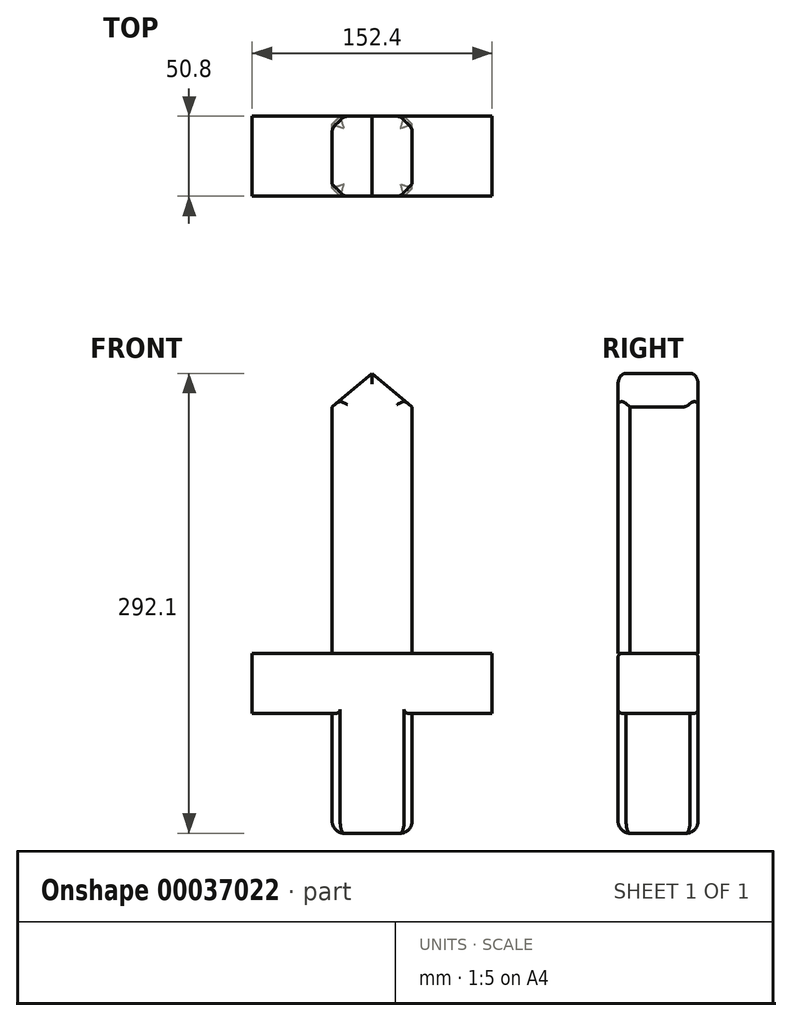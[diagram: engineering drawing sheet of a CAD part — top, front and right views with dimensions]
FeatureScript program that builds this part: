
annotation { "Feature Type Name" : "Feature", "Feature Type Description" : "" }
export const myFeature = defineFeature(function(context is Context, id is Id, definition is map)
    precondition{}
    {
        {
            var Q0;
            Q0=qCreatedBy(makeId("Top.planeOp"),FACE);
            var sketch = newSketch(context, id + "F0", { "sketchPlane" : qUnion([Q0])});
            skLineSegment(sketch, "E0.bottom", {"start": v(0, 0) * mm, "end": v(50.8, 0) * mm});
            skLineSegment(sketch, "E0.top", {"start": v(0, 50.8) * mm, "end": v(50.8, 50.8) * mm});
            skLineSegment(sketch, "E0.left", {"start": v(0, 0) * mm, "end": v(0, 50.8) * mm});
            skLineSegment(sketch, "E0.right", {"start": v(50.8, 0) * mm, "end": v(50.8, 50.8) * mm});
            skSolve(sketch);
        }
        {
            var Q0;
            Q0 = qSketchRegion(id + "F0", true);
            extrude(context, id + "F1", {"entities" : qUnion([Q0]), "depth" : 76.2 * mm});
        }
        {
            var Q0;
            Q0=makeQuery(id+"F1.opExtrude","CAP_FACE",FACE,{"disambiguationData":[OSD([sQuery(id+"F0.wireOp",EDGE,"E0.bottom"),sQuery(id+"F0.wireOp",EDGE,"E0.top"),sQuery(id+"F0.wireOp",EDGE,"E0.left"),sQuery(id+"F0.wireOp",EDGE,"E0.right")])],"isStart":false});
            var sketch = newSketch(context, id + "F2", { "sketchPlane" : qUnion([Q0])});
            skLineSegment(sketch, "E1.bottom", {"start": v(0, 0) * mm, "end": v(50.8, 0) * mm});
            skLineSegment(sketch, "E1.top", {"start": v(0, 50.8) * mm, "end": v(50.8, 50.8) * mm});
            skLineSegment(sketch, "E1.left", {"start": v(0, 0) * mm, "end": v(0, 50.8) * mm});
            skLineSegment(sketch, "E1.right", {"start": v(50.8, 0) * mm, "end": v(50.8, 50.8) * mm});
            skLineSegment(sketch, "E2.rect.bottom", {"start": v(101.6, 0) * mm, "end": v(-50.8, 0) * mm});
            skLineSegment(sketch, "E2.rect.top", {"start": v(101.6, 50.8) * mm, "end": v(-50.8, 50.8) * mm});
            skLineSegment(sketch, "E2.rect.left", {"start": v(101.6, 0) * mm, "end": v(101.6, 50.8) * mm});
            skLineSegment(sketch, "E2.rect.right", {"start": v(-50.8, 0) * mm, "end": v(-50.8, 50.8) * mm});
            skPoint(sketch, "E2.rect.middle", {"position": v(25.4, 25.4) * mm});
            skPoint(sketch, "E2.rect.middle.positionSnap0", {"position": v(50.8, 25.4) * mm});
            skPoint(sketch, "E2.rect.middle.positionSnap1", {"position": v(25.4, 50.8) * mm});
            skPoint(sketch, "E2.rect.centerSnap0", {"position": v(50.8, 25.4) * mm});
            skPoint(sketch, "E2.rect.centerSnap1", {"position": v(25.4, 50.8) * mm});
            skSolve(sketch);
        }
        {
            var Q0;
            {var subQ2=sQuery(id+"F2.wireOp",EDGE,"E1.left");Q0=makeQuery(id+"F2.imprint","IMPRINT",FACE,{"disambiguationData":[TD([[makeQuery(id+"F2.imprint","IMPRINT",EDGE,{"derivedFrom":subQ2}),1.0]])]});}
            var Q1;
            {var subQ2=sQuery(id+"F2.wireOp",EDGE,"E1.left");Q1=makeQuery(id+"F2.imprint","IMPRINT",FACE,{"disambiguationData":[TD([[makeQuery(id+"F2.imprint","IMPRINT",EDGE,{"derivedFrom":subQ2}),-1.0]])]});}
            var Q2;
            {var subQ2=sQuery(id+"F2.wireOp",EDGE,"E1.right");Q2=makeQuery(id+"F2.imprint","IMPRINT",FACE,{"disambiguationData":[TD([[makeQuery(id+"F2.imprint","IMPRINT",EDGE,{"derivedFrom":subQ2}),-1.0]])]});}
            extrude(context, id + "F3", {"entities" : qUnion([Q0, Q1, Q2]), "operationType" : NewBodyOperationType.ADD, "depth" : 38.1 * mm});
        }
        {
            var Q0;
            Q0=makeQuery(id+"F3.boolean.opBoolean","MERGE",FACE,{"derivedFrom":[makeQuery(id+"F1.opExtrude","SWEPT_FACE",FACE,{"disambiguationData":[OSD([sQuery(id+"F0.wireOp",EDGE,"E0.bottom")])]}),makeQuery(id+"F3.opExtrude","SWEPT_FACE",FACE,{"disambiguationData":[OSD([sQuery(id+"F2.wireOp",EDGE,"E2.rect.bottom")])]})]});
            var sketch = newSketch(context, id + "F4", { "sketchPlane" : qUnion([Q0])});
            skLineSegment(sketch, "E3.bottom", {"start": v(0, 114.3) * mm, "end": v(50.8, 114.3) * mm});
            skLineSegment(sketch, "E3.left", {"start": v(0, 114.3) * mm, "end": v(0, 270.79) * mm});
            skLineSegment(sketch, "E3.right", {"start": v(50.8, 114.3) * mm, "end": v(50.8, 270.79) * mm});
            skLineSegment(sketch, "E4", {"start": v(25.4, 292.1) * mm, "end": v(0, 270.79) * mm});
            skLineSegment(sketch, "E5", {"start": v(25.4, 292.1) * mm, "end": v(50.8, 270.79) * mm});
            skPoint(sketch, "E6.orphan", {"position": v(0, 292.1) * mm});
            skPoint(sketch, "E3.top.end.orphan", {"position": v(50.8, 292.1) * mm});
            skSolve(sketch);
        }
        {
            var Q0;
            Q0=makeQuery(id+"F4.imprint","IMPRINT",FACE,{"disambiguationData":[TD([[makeQuery(id+"F4.imprint","IMPRINT",EDGE,{"derivedFrom":sQuery(id+"F4.wireOp",EDGE,"E3.bottom")}),-1.0]])]});
            extrude(context, id + "F5", {"entities" : qUnion([Q0]), "oppositeDirection" : true, "depth" : 50.8 * mm});
        }
        {
            var Q0;
            Q0=makeQuery(id+"F5.opExtrude","CAP_EDGE",EDGE,{"disambiguationData":[OSD([sQuery(id+"F4.wireOp",EDGE,"E3.left")])],"isStart":false});
            var Q1;
            Q1=makeQuery(id+"F5.opExtrude","CAP_EDGE",EDGE,{"disambiguationData":[OSD([sQuery(id+"F4.wireOp",EDGE,"E3.right")])],"isStart":false});
            var Q2;
            Q2=makeQuery(id+"F5.opExtrude","CAP_EDGE",EDGE,{"disambiguationData":[OSD([sQuery(id+"F4.wireOp",EDGE,"E3.left")])],"isStart":true});
            var Q3;
            Q3=makeQuery(id+"F5.opExtrude","CAP_EDGE",EDGE,{"disambiguationData":[OSD([sQuery(id+"F4.wireOp",EDGE,"E3.right")])],"isStart":true});
            chamfer(context, id + "F6", {"entities" : qUnion([Q0, Q1, Q2, Q3]), "width" : 7.62 * mm, "tangentPropagation" : true});
        }
        {
            var Q0;
            Q0=makeQuery(id+"F1.opExtrude","CAP_FACE",FACE,{"disambiguationData":[OSD([sQuery(id+"F0.wireOp",EDGE,"E0.bottom"),sQuery(id+"F0.wireOp",EDGE,"E0.top"),sQuery(id+"F0.wireOp",EDGE,"E0.left"),sQuery(id+"F0.wireOp",EDGE,"E0.right")])],"isStart":true});
            var sketch = newSketch(context, id + "F7", { "sketchPlane" : qUnion([Q0])});
            skLineSegment(sketch, "E7", {"start": v(25.4, 0) * mm, "end": v(25.4, -50.8) * mm, "construction": true});
            skArc(sketch, "E8", {"start": v(25.4, -50.8) * mm, "mid": v(50.8, -25.4) * mm, "end": v(25.4, 0) * mm});
            skSolve(sketch);
        }
        {
            var Q0;
            Q0=sQuery(id+"F7.wireOp",EDGE,"E8");
            var Q1;
            Q1=sQuery(id+"F7.wireOp",EDGE,"E7");
            revolve(context, id + "F8", {"bodyType" : ToolBodyType.SURFACE, "surfaceEntities" : qUnion([Q0]), "axis" : qUnion([Q1]), "revolveType" : RevolveType.FULL});
        }
        {
            var Q0;
            Q0=makeQuery(id+"F1.opExtrude","CAP_EDGE",EDGE,{"disambiguationData":[OSD([sQuery(id+"F0.wireOp",EDGE,"E0.right")])],"isStart":true});
            var Q1;
            Q1=makeQuery(id+"F1.opExtrude","CAP_EDGE",EDGE,{"disambiguationData":[OSD([sQuery(id+"F0.wireOp",EDGE,"E0.bottom")])],"isStart":true});
            var Q2;
            Q2=makeQuery(id+"F1.opExtrude","CAP_EDGE",EDGE,{"disambiguationData":[OSD([sQuery(id+"F0.wireOp",EDGE,"E0.left")])],"isStart":true});
            var Q3;
            Q3=makeQuery(id+"F1.opExtrude","CAP_EDGE",EDGE,{"disambiguationData":[OSD([sQuery(id+"F0.wireOp",EDGE,"E0.top")])],"isStart":true});
            fillet(context, id + "F9", {"entities" : qUnion([Q0, Q1, Q2, Q3]), "radius" : 7.62 * mm, "tangentPropagation" : true, "allowEdgeOverflow" : false});
        }
        {
            var Q0;
            Q0=makeQuery(id+"F1.opExtrude","SWEPT_EDGE",EDGE,{"disambiguationData":[OSD([sQuery(id+"F0.wireOp",EDGE,"E0.top"),sQuery(id+"F0.wireOp",EDGE,"E0.left")])]});
            var Q1;
            Q1=makeQuery(id+"F1.opExtrude","SWEPT_EDGE",EDGE,{"disambiguationData":[OSD([sQuery(id+"F0.wireOp",EDGE,"E0.top"),sQuery(id+"F0.wireOp",EDGE,"E0.right")])]});
            var Q2;
            Q2=makeQuery(id+"F1.opExtrude","SWEPT_EDGE",EDGE,{"disambiguationData":[OSD([sQuery(id+"F0.wireOp",EDGE,"E0.bottom"),sQuery(id+"F0.wireOp",EDGE,"E0.left")])]});
            var Q3;
            Q3=makeQuery(id+"F1.opExtrude","SWEPT_EDGE",EDGE,{"disambiguationData":[OSD([sQuery(id+"F0.wireOp",EDGE,"E0.bottom"),sQuery(id+"F0.wireOp",EDGE,"E0.right")])]});
            chamfer(context, id + "F10", {"entities" : qUnion([Q0, Q1, Q2, Q3]), "width" : 5.08 * mm, "tangentPropagation" : true});
        }
        {
            var Q0;
            Q0=makeQuery(id+"F3.opExtrude","CAP_EDGE",EDGE,{"disambiguationData":[OSD([sQuery(id+"F2.wireOp",EDGE,"E2.rect.top")])],"isStart":false});
            var Q1;
            {var subQ0=sQuery(id+"F2.wireOp",EDGE,"E2.rect.top");Q1=makeQuery(id+"F3.boolean.opBoolean","SPLIT",EDGE,{"disambiguationData":[TD([makeQuery(id+"F1.opExtrude","SWEPT_FACE",FACE,{"disambiguationData":[OSD([sQuery(id+"F0.wireOp",EDGE,"E0.left")])]})])],"derivedFrom":makeQuery(id+"F3.opExtrude","CAP_EDGE",EDGE,{"disambiguationData":[OSD([subQ0])],"isStart":true})});}
            var Q2;
            {var subQ0=sQuery(id+"F2.wireOp",EDGE,"E2.rect.top");Q2=makeQuery(id+"F3.boolean.opBoolean","SPLIT",EDGE,{"disambiguationData":[TD([makeQuery(id+"F1.opExtrude","SWEPT_FACE",FACE,{"disambiguationData":[OSD([sQuery(id+"F0.wireOp",EDGE,"E0.right")])]})])],"derivedFrom":makeQuery(id+"F3.opExtrude","CAP_EDGE",EDGE,{"disambiguationData":[OSD([subQ0])],"isStart":true})});}
            var Q3;
            Q3=makeQuery(id+"F3.opExtrude","CAP_EDGE",EDGE,{"disambiguationData":[OSD([sQuery(id+"F2.wireOp",EDGE,"E2.rect.bottom")])],"isStart":false});
            var Q4;
            {var subQ0=sQuery(id+"F2.wireOp",EDGE,"E2.rect.bottom");Q4=makeQuery(id+"F3.boolean.opBoolean","SPLIT",EDGE,{"disambiguationData":[TD([makeQuery(id+"F1.opExtrude","SWEPT_FACE",FACE,{"disambiguationData":[OSD([sQuery(id+"F0.wireOp",EDGE,"E0.left")])]})])],"derivedFrom":makeQuery(id+"F3.opExtrude","CAP_EDGE",EDGE,{"disambiguationData":[OSD([subQ0])],"isStart":true})});}
            var Q5;
            {var subQ0=sQuery(id+"F2.wireOp",EDGE,"E2.rect.bottom");Q5=makeQuery(id+"F3.boolean.opBoolean","SPLIT",EDGE,{"disambiguationData":[TD([makeQuery(id+"F1.opExtrude","SWEPT_FACE",FACE,{"disambiguationData":[OSD([sQuery(id+"F0.wireOp",EDGE,"E0.right")])]})])],"derivedFrom":makeQuery(id+"F3.opExtrude","CAP_EDGE",EDGE,{"disambiguationData":[OSD([subQ0])],"isStart":true})});}
            fillet(context, id + "F11", {"entities" : qUnion([Q0, Q1, Q2, Q3, Q4, Q5]), "radius" : 2.54 * mm, "tangentPropagation" : true, "allowEdgeOverflow" : false});
        }
        {
            var Q0;
            {var subQ0=sQuery(id+"F4.wireOp",EDGE,"E3.right");Q0=makeQuery(id+"F6.opChamfer","BLEND_EDGE",EDGE,{"blendedFrom":[makeQuery(id+"F5.opExtrude","CAP_EDGE",EDGE,{"disambiguationData":[OSD([subQ0])],"isStart":true}),makeQuery(id+"F5.opExtrude","CAP_FACE",FACE,{"disambiguationData":[OSD([sQuery(id+"F4.wireOp",EDGE,"E3.bottom"),sQuery(id+"F4.wireOp",EDGE,"E3.left"),subQ0,sQuery(id+"F4.wireOp",EDGE,"E4"),sQuery(id+"F4.wireOp",EDGE,"E5")])],"isStart":true})],"blendedInto":[makeQuery(id+"F5.opExtrude","CAP_FACE",FACE,{"disambiguationData":[OSD([sQuery(id+"F4.wireOp",EDGE,"E3.bottom"),sQuery(id+"F4.wireOp",EDGE,"E3.left"),subQ0,sQuery(id+"F4.wireOp",EDGE,"E4"),sQuery(id+"F4.wireOp",EDGE,"E5")])],"isStart":true})]});}
            var Q1;
            Q1=makeQuery(id+"F5.opExtrude","CAP_EDGE",EDGE,{"disambiguationData":[OSD([sQuery(id+"F4.wireOp",EDGE,"E5")])],"isStart":true});
            var Q2;
            Q2=makeQuery(id+"F5.opExtrude","CAP_EDGE",EDGE,{"disambiguationData":[OSD([sQuery(id+"F4.wireOp",EDGE,"E4")])],"isStart":true});
            var Q3;
            {var subQ0=sQuery(id+"F4.wireOp",EDGE,"E3.left");Q3=makeQuery(id+"F6.opChamfer","BLEND_EDGE",EDGE,{"blendedFrom":[makeQuery(id+"F5.opExtrude","CAP_EDGE",EDGE,{"disambiguationData":[OSD([subQ0])],"isStart":true}),makeQuery(id+"F5.opExtrude","CAP_FACE",FACE,{"disambiguationData":[OSD([sQuery(id+"F4.wireOp",EDGE,"E3.bottom"),subQ0,sQuery(id+"F4.wireOp",EDGE,"E3.right"),sQuery(id+"F4.wireOp",EDGE,"E4"),sQuery(id+"F4.wireOp",EDGE,"E5")])],"isStart":true})],"blendedInto":[makeQuery(id+"F5.opExtrude","CAP_FACE",FACE,{"disambiguationData":[OSD([sQuery(id+"F4.wireOp",EDGE,"E3.bottom"),subQ0,sQuery(id+"F4.wireOp",EDGE,"E3.right"),sQuery(id+"F4.wireOp",EDGE,"E4"),sQuery(id+"F4.wireOp",EDGE,"E5")])],"isStart":true})]});}
            var Q4;
            {var subQ0=sQuery(id+"F4.wireOp",EDGE,"E3.right");Q4=makeQuery(id+"F6.opChamfer","BLEND_EDGE",EDGE,{"blendedFrom":[makeQuery(id+"F5.opExtrude","CAP_EDGE",EDGE,{"disambiguationData":[OSD([subQ0])],"isStart":false}),makeQuery(id+"F5.opExtrude","SWEPT_FACE",FACE,{"disambiguationData":[OSD([subQ0])]})],"blendedInto":[makeQuery(id+"F5.opExtrude","SWEPT_FACE",FACE,{"disambiguationData":[OSD([subQ0])]})]});}
            var Q5;
            {var subQ0=sQuery(id+"F4.wireOp",EDGE,"E3.right");Q5=makeQuery(id+"F6.opChamfer","BLEND_EDGE",EDGE,{"blendedFrom":[makeQuery(id+"F5.opExtrude","CAP_EDGE",EDGE,{"disambiguationData":[OSD([subQ0])],"isStart":false}),makeQuery(id+"F5.opExtrude","CAP_FACE",FACE,{"disambiguationData":[OSD([sQuery(id+"F4.wireOp",EDGE,"E3.bottom"),sQuery(id+"F4.wireOp",EDGE,"E3.left"),subQ0,sQuery(id+"F4.wireOp",EDGE,"E4"),sQuery(id+"F4.wireOp",EDGE,"E5")])],"isStart":false})],"blendedInto":[makeQuery(id+"F5.opExtrude","CAP_FACE",FACE,{"disambiguationData":[OSD([sQuery(id+"F4.wireOp",EDGE,"E3.bottom"),sQuery(id+"F4.wireOp",EDGE,"E3.left"),subQ0,sQuery(id+"F4.wireOp",EDGE,"E4"),sQuery(id+"F4.wireOp",EDGE,"E5")])],"isStart":false})]});}
            var Q6;
            {var subQ0=sQuery(id+"F4.wireOp",EDGE,"E3.left");Q6=makeQuery(id+"F6.opChamfer","BLEND_EDGE",EDGE,{"blendedFrom":[makeQuery(id+"F5.opExtrude","CAP_EDGE",EDGE,{"disambiguationData":[OSD([subQ0])],"isStart":false}),makeQuery(id+"F5.opExtrude","SWEPT_FACE",FACE,{"disambiguationData":[OSD([subQ0])]})],"blendedInto":[makeQuery(id+"F5.opExtrude","SWEPT_FACE",FACE,{"disambiguationData":[OSD([subQ0])]})]});}
            var Q7;
            {var subQ0=sQuery(id+"F4.wireOp",EDGE,"E3.left");Q7=makeQuery(id+"F6.opChamfer","BLEND_EDGE",EDGE,{"blendedFrom":[makeQuery(id+"F5.opExtrude","CAP_EDGE",EDGE,{"disambiguationData":[OSD([subQ0])],"isStart":false}),makeQuery(id+"F5.opExtrude","CAP_FACE",FACE,{"disambiguationData":[OSD([sQuery(id+"F4.wireOp",EDGE,"E3.bottom"),subQ0,sQuery(id+"F4.wireOp",EDGE,"E3.right"),sQuery(id+"F4.wireOp",EDGE,"E4"),sQuery(id+"F4.wireOp",EDGE,"E5")])],"isStart":false})],"blendedInto":[makeQuery(id+"F5.opExtrude","CAP_FACE",FACE,{"disambiguationData":[OSD([sQuery(id+"F4.wireOp",EDGE,"E3.bottom"),subQ0,sQuery(id+"F4.wireOp",EDGE,"E3.right"),sQuery(id+"F4.wireOp",EDGE,"E4"),sQuery(id+"F4.wireOp",EDGE,"E5")])],"isStart":false})]});}
            var Q8;
            Q8=makeQuery(id+"F5.opExtrude","CAP_EDGE",EDGE,{"disambiguationData":[OSD([sQuery(id+"F4.wireOp",EDGE,"E4")])],"isStart":false});
            var Q9;
            Q9=makeQuery(id+"F5.opExtrude","CAP_EDGE",EDGE,{"disambiguationData":[OSD([sQuery(id+"F4.wireOp",EDGE,"E5")])],"isStart":false});
            fillet(context, id + "F12", {"entities" : qUnion([Q0, Q1, Q2, Q3, Q4, Q5, Q6, Q7, Q8, Q9]), "radius" : 5.08 * mm, "tangentPropagation" : true, "allowEdgeOverflow" : false});
        }
    });
